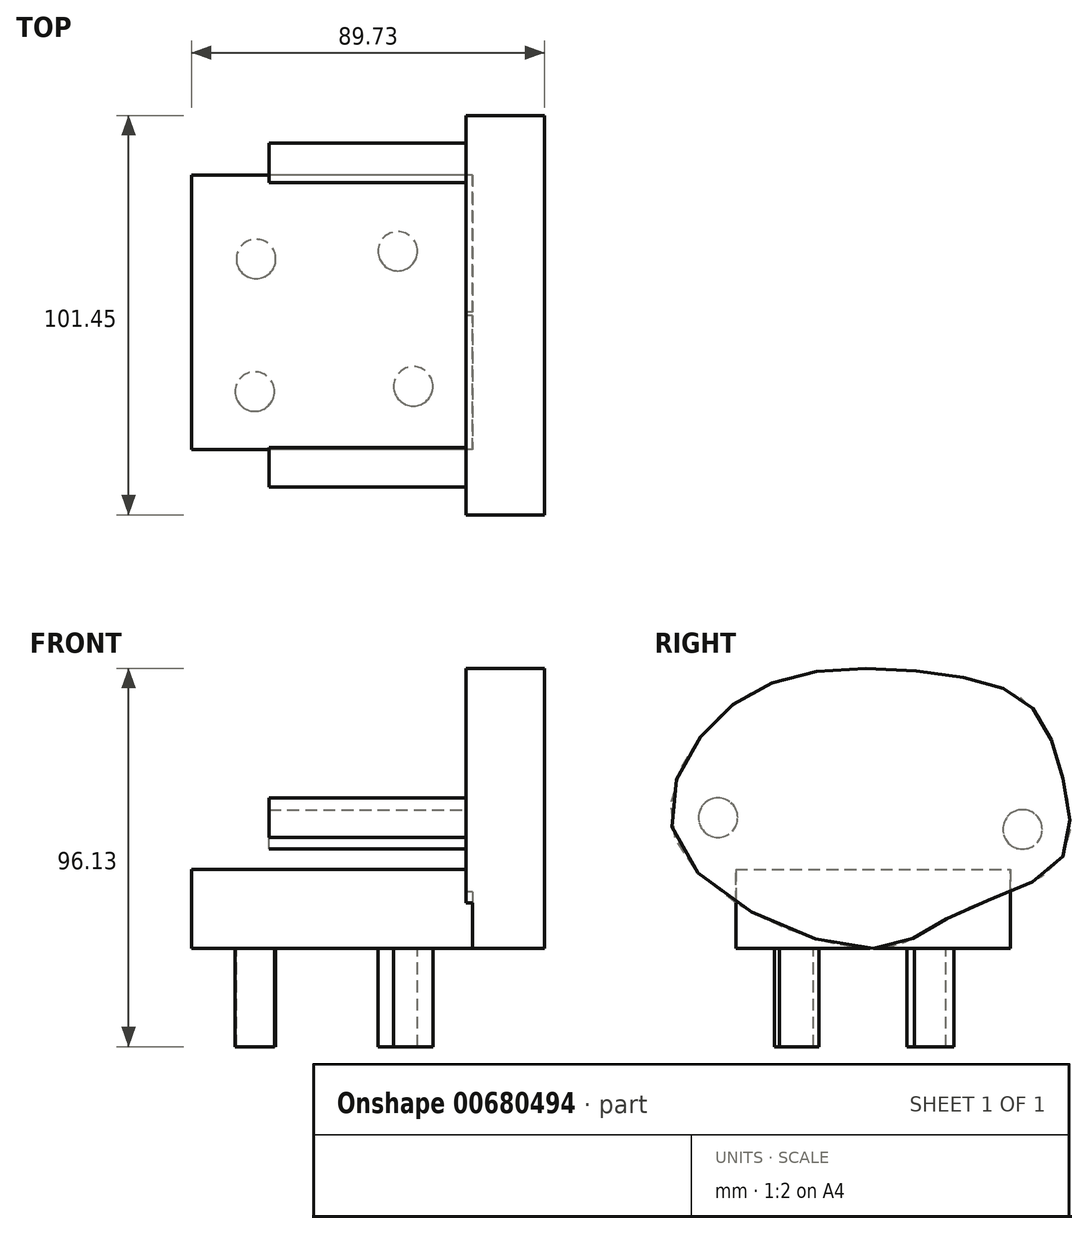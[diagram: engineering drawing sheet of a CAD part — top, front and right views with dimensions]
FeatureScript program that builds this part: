
annotation { "Feature Type Name" : "Feature", "Feature Type Description" : "" }
export const myFeature = defineFeature(function(context is Context, id is Id, definition is map)
    precondition{}
    {
        {
            var Q0;
            Q0=qCreatedBy(makeId("Top.planeOp"),FACE);
            var sketch = newSketch(context, id + "F0", { "sketchPlane" : qUnion([Q0])});
            skLineSegment(sketch, "E0.bottom", {"start": v(35.73, -34.89) * mm, "end": v(-35.73, -34.89) * mm});
            skLineSegment(sketch, "E0.top", {"start": v(35.73, 34.89) * mm, "end": v(-35.73, 34.89) * mm});
            skLineSegment(sketch, "E0.left", {"start": v(35.73, -34.89) * mm, "end": v(35.73, 34.89) * mm});
            skLineSegment(sketch, "E0.right", {"start": v(-35.73, -34.89) * mm, "end": v(-35.73, 34.89) * mm});
            skPoint(sketch, "E0.middle", {"position": v(0, 0) * mm});
            skSolve(sketch);
        }
        {
            var Q0;
            Q0=makeQuery(id+"F0.imprint","IMPRINT",FACE,{"disambiguationData":[TD([[makeQuery(id+"F0.imprint","IMPRINT",EDGE,{"derivedFrom":sQuery(id+"F0.wireOp",EDGE,"E0.bottom")}),-1.0]])]});
            extrude(context, id + "F1", {"entities" : qUnion([Q0]), "depth" : 20 * mm, "offsetDistance" : 25 * mm});
        }
        {
            var Q0;
            Q0=qCreatedBy(makeId("Right.planeOp"),FACE);
            cPlane(context, id + "F2", {"entities" : qUnion([Q0]), "cplaneType" : CPlaneType.OFFSET, "offset" : 34 * mm, "width" : 150 * mm, "height" : 150 * mm});
        }
        {
            var Q0;
            Q0=qCreatedBy(id+"F2.planeOp",FACE);
            var sketch = newSketch(context, id + "F3", { "sketchPlane" : qUnion([Q0])});
            skFitSpline(sketch, "E1", {"points": [v(0, 0) * mm, v(-49.03, 25.1) * mm, v(-42.76, 55.14) * mm, v(-18, 69.67) * mm, v(17.33, 69.67) * mm, v(39.46, 62.08) * mm, v(48.04, 43.58) * mm, v(47.38, 22.12) * mm, v(21.3, 8.92) * mm, v(0, 0) * mm]});
            skSolve(sketch);
        }
        {
            var Q0;
            Q0=makeQuery(id+"F3.imprint","IMPRINT",FACE,{"disambiguationData":[TD([[makeQuery(id+"F3.imprint","IMPRINT",EDGE,{"derivedFrom":sQuery(id+"F3.wireOp",EDGE,"E1")}),-1.0]])]});
            extrude(context, id + "F4", {"entities" : qUnion([Q0]), "operationType" : NewBodyOperationType.ADD, "depth" : 20 * mm, "offsetDistance" : 25 * mm});
        }
        {
            var Q0;
            Q0=makeQuery(id+"F1.opExtrude","CAP_FACE",FACE,{"disambiguationData":[OSD([sQuery(id+"F0.wireOp",EDGE,"E0.bottom"),sQuery(id+"F0.wireOp",EDGE,"E0.top"),sQuery(id+"F0.wireOp",EDGE,"E0.left"),sQuery(id+"F0.wireOp",EDGE,"E0.right")])],"isStart":true});
            var sketch = newSketch(context, id + "F5", { "sketchPlane" : qUnion([Q0])});
            skCircle(sketch, "E2", {"center": v(-19.65, 20.14) * mm, "radius": 5 * mm});
            skSolve(sketch);
        }
        {
            var Q0;
            Q0=makeQuery(id+"F5.imprint","IMPRINT",FACE,{"disambiguationData":[TD([[makeQuery(id+"F5.imprint","IMPRINT",EDGE,{"derivedFrom":sQuery(id+"F5.wireOp",EDGE,"E2")}),1.0]])]});
            extrude(context, id + "F6", {"entities" : qUnion([Q0]), "operationType" : NewBodyOperationType.ADD, "depth" : 25 * mm, "offsetDistance" : 25 * mm});
        }
        {
            var Q0;
            Q0=makeQuery(id+"F1.opExtrude","CAP_FACE",FACE,{"disambiguationData":[OSD([sQuery(id+"F0.wireOp",EDGE,"E0.bottom"),sQuery(id+"F0.wireOp",EDGE,"E0.top"),sQuery(id+"F0.wireOp",EDGE,"E0.left"),sQuery(id+"F0.wireOp",EDGE,"E0.right")])],"isStart":true});
            var sketch = newSketch(context, id + "F7", { "sketchPlane" : qUnion([Q0])});
            skCircle(sketch, "E3", {"center": v(-19.32, -13.54) * mm, "radius": 5 * mm});
            skSolve(sketch);
        }
        {
            var Q0;
            Q0 = qSketchRegion(id + "F7", true);
            extrude(context, id + "F8", {"entities" : qUnion([Q0]), "operationType" : NewBodyOperationType.ADD, "depth" : 25 * mm, "offsetDistance" : 25 * mm});
        }
        {
            var Q0;
            Q0=makeQuery(id+"F1.opExtrude","CAP_FACE",FACE,{"disambiguationData":[OSD([sQuery(id+"F0.wireOp",EDGE,"E0.bottom"),sQuery(id+"F0.wireOp",EDGE,"E0.top"),sQuery(id+"F0.wireOp",EDGE,"E0.left"),sQuery(id+"F0.wireOp",EDGE,"E0.right")])],"isStart":true});
            var sketch = newSketch(context, id + "F9", { "sketchPlane" : qUnion([Q0])});
            skCircle(sketch, "E4", {"center": v(20.64, 18.82) * mm, "radius": 5 * mm});
            skSolve(sketch);
        }
        {
            var Q0;
            Q0=makeQuery(id+"F9.imprint","IMPRINT",FACE,{"disambiguationData":[TD([[makeQuery(id+"F9.imprint","IMPRINT",EDGE,{"derivedFrom":sQuery(id+"F9.wireOp",EDGE,"E4")}),1.0]])]});
            var Q1;
            Q1=sQuery(id+"F9.wireOp",EDGE,"E4");
            extrude(context, id + "F10", {"entities" : qUnion([Q0]), "operationType" : NewBodyOperationType.ADD, "surfaceEntities" : qUnion([Q1]), "depth" : 25 * mm, "offsetDistance" : 25 * mm});
        }
        {
            var Q0;
            Q0=makeQuery(id+"F1.opExtrude","CAP_FACE",FACE,{"disambiguationData":[OSD([sQuery(id+"F0.wireOp",EDGE,"E0.bottom"),sQuery(id+"F0.wireOp",EDGE,"E0.top"),sQuery(id+"F0.wireOp",EDGE,"E0.left"),sQuery(id+"F0.wireOp",EDGE,"E0.right")])],"isStart":true});
            var sketch = newSketch(context, id + "F11", { "sketchPlane" : qUnion([Q0])});
            skCircle(sketch, "E5", {"center": v(16.67, -15.52) * mm, "radius": 5 * mm});
            skSolve(sketch);
        }
        {
            var Q0;
            Q0=makeQuery(id+"F11.imprint","IMPRINT",FACE,{"disambiguationData":[TD([[makeQuery(id+"F11.imprint","IMPRINT",EDGE,{"derivedFrom":sQuery(id+"F11.wireOp",EDGE,"E5")}),1.0]])]});
            var Q1;
            Q1=sQuery(id+"F11.wireOp",EDGE,"E5");
            extrude(context, id + "F12", {"entities" : qUnion([Q0]), "operationType" : NewBodyOperationType.ADD, "surfaceEntities" : qUnion([Q1]), "depth" : 25 * mm, "offsetDistance" : 25 * mm});
        }
        {
            var Q0;
            Q0=makeQuery(id+"F4.opExtrude","CAP_FACE",FACE,{"disambiguationData":[OSD([sQuery(id+"F3.wireOp",EDGE,"E1")])],"isStart":true});
            var sketch = newSketch(context, id + "F13", { "sketchPlane" : qUnion([Q0])});
            skCircle(sketch, "E6", {"center": v(-37.95, 30.2) * mm, "radius": 5 * mm});
            skSolve(sketch);
        }
        {
            var Q0;
            Q0=makeQuery(id+"F13.imprint","IMPRINT",FACE,{"disambiguationData":[TD([[makeQuery(id+"F13.imprint","IMPRINT",EDGE,{"derivedFrom":sQuery(id+"F13.wireOp",EDGE,"E6")}),1.0]])]});
            var Q1;
            Q1=sQuery(id+"F13.wireOp",EDGE,"E6");
            extrude(context, id + "F14", {"entities" : qUnion([Q0]), "operationType" : NewBodyOperationType.ADD, "surfaceEntities" : qUnion([Q1]), "depth" : 50 * mm, "offsetDistance" : 25 * mm});
        }
        {
            var Q0;
            Q0=makeQuery(id+"F4.opExtrude","CAP_FACE",FACE,{"disambiguationData":[OSD([sQuery(id+"F3.wireOp",EDGE,"E1")])],"isStart":true});
            var sketch = newSketch(context, id + "F15", { "sketchPlane" : qUnion([Q0])});
            skCircle(sketch, "E7", {"center": v(39.41, 33.2) * mm, "radius": 5 * mm});
            skSolve(sketch);
        }
        {
            var Q0;
            Q0=makeQuery(id+"F15.imprint","IMPRINT",FACE,{"disambiguationData":[TD([[makeQuery(id+"F15.imprint","IMPRINT",EDGE,{"derivedFrom":sQuery(id+"F15.wireOp",EDGE,"E7")}),1.0]])]});
            var Q1;
            Q1=sQuery(id+"F15.wireOp",EDGE,"E7");
            extrude(context, id + "F16", {"entities" : qUnion([Q0]), "operationType" : NewBodyOperationType.ADD, "surfaceEntities" : qUnion([Q1]), "depth" : 50 * mm, "offsetDistance" : 25 * mm});
        }
    });
